# Revit family: TL 2D_Tracklok_Flat_SPT-10F
name_source: partatom
category: Detail Items
revit_build: Autodesk Revit 2016 (Build: 20150714_1515(x64)
units: mm (PartAtom-declared; Revit-internal decimal feet)

## family parameters
Rotate with component = No
Shared = No

## types (12) — shared parameters

## per-type parameters (varying)
| type | Flat End Elevation | Flat Plan | Flat Side Elevation | Gaplok End | Gaplok Plan | Gaplok Side | Tracklok Retro | Tracklok Retro-Plan | Tracklok Timba | Tracklok Timba - Plan |
| Flat-Std-Side Elev | No | No | Yes | No | No | No | No | No | No | No |
| Flat-Std-Plan | No | Yes | No | No | No | No | No | No | No | No |
| Flat-Std-End Elev | Yes | No | No | No | No | No | No | No | No | No |
| Flat-Retro-Side Elev | No | No | Yes | No | No | No | Yes | No | No | No |
| Flat-Retro-End Elev | Yes | No | No | No | No | No | Yes | No | No | No |
| Flat-Retro-Plan | No | Yes | No | No | No | No | No | Yes | No | No |
| Flat-Timba-Plan | No | Yes | No | No | No | No | No | No | No | Yes |
| Flat-Timba-End Elev | Yes | No | No | No | No | No | No | No | Yes | No |
| Flat-Timba-Side Elev | No | No | Yes | No | No | No | No | No | Yes | No |
| Flat-Gaplok-End | Yes | No | No | No | No | Yes | No | No | No | No |
| Flat-Gaplok-Side | No | No | Yes | Yes | No | No | No | No | No | No |
| Flat-Gaplok-Plan | No | Yes | No | No | Yes | No | No | No | No | No |

## geometry (parser evidence)
native form markers: Sweep x1
no freeform markers — native parametric forms only
